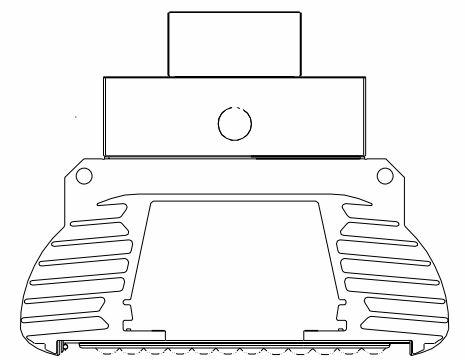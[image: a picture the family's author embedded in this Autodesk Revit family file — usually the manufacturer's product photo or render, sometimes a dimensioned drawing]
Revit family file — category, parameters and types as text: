
# Revit family: LLHP2
name_source: partatom
category: Lighting Fixtures
revit_build: Autodesk Revit Architecture 2012 (Build: 20110309_2315(x64)
units: mm (PartAtom-declared; Revit-internal decimal feet)

## types (6) — shared parameters
Apparent Load = 0 VA
Backbox = White
Color Filter = 16777215
Default Elevation = 4' - 0"
Description = LLHP is a long-life high-efficiency LED high bay product that meets the most restrictive lighting power density codes and typically qualifies for utility rebate programs.
Dimming Lamp Color Temperature Shift = <None>
Driver = 0-10V Dimming
Emit from Line Length = 1' - 0"
Glass = White Glass
Lamp = LED
Manufacturer = Columbia Lighting
Manufacturer Fax = (866)-898-1065
Model = LLHP2
Product Documentation Link = http://www.columbialighting.com
Product Page URL = http://www.columbialighting.com
Tilt Angle = -90.00°
URL = http://www.columbialighting.com
Voltage = 120 V

## per-type parameters (varying)
| type | Distribution | Lumen Output | Nominal watts | Photometric Web File |
| LLHP2-50-L-A-EDU | Aisle | Low Lumen | 143 W | LLHP2-50-L-A-EDU.ies |
| LLHP2-50-H-A-EDU | Aisle | High Lumen | 281 W | LLHP2-50-H-A-EDU.ies |
| LLHP2-50-L-M-EDU | Medium | Low Lumen | 143 W | LLHP2-50-L-M-EDU.ies |
| LLHP2-50-L-W-EDU | Wide | Low Lumen | 143 W | LLHP2-50-L-W-EDU.ies |
| LLHP2-50-H-M-EDU | Medium | High Lumen | 281 W | LLHP2-50-H-M-EDU.ies |
| LLHP2-50-H-W-EDU | Wide | High Lumen | 281 W | LLHP2-50-H-W-EDU.ies |

## geometry (parser evidence)
native form markers: Sweep x4
no freeform markers — native parametric forms only
